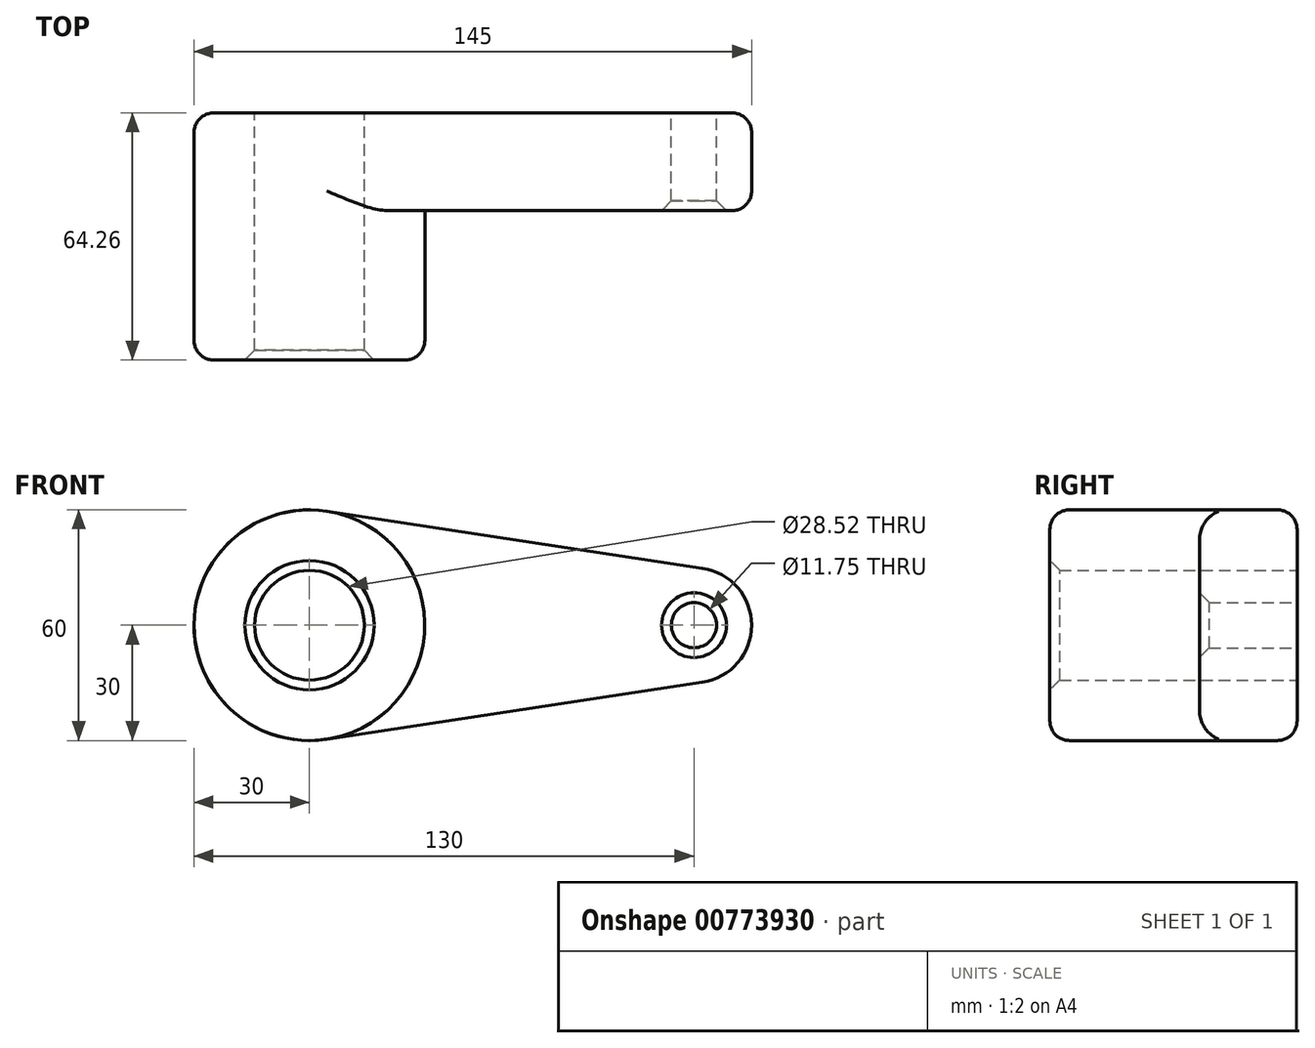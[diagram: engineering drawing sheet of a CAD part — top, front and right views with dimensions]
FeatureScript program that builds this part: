
annotation { "Feature Type Name" : "Feature", "Feature Type Description" : "" }
export const myFeature = defineFeature(function(context is Context, id is Id, definition is map)
    precondition{}
    {
        {
            var Q0;
            Q0=qCreatedBy(makeId("Front.planeOp"),FACE);
            var sketch = newSketch(context, id + "F0", { "sketchPlane" : qUnion([Q0])});
            skCircle(sketch, "E0", {"center": v(0, 0) * mm, "radius": 30 * mm});
            skCircle(sketch, "E1", {"center": v(100, 0) * mm, "radius": 15 * mm});
            skLineSegment(sketch, "E2", {"start": v(4.5, 29.66) * mm, "end": v(102.25, 14.83) * mm});
            skLineSegment(sketch, "E3", {"start": v(4.5, -29.66) * mm, "end": v(102.25, -14.83) * mm});
            skCircle(sketch, "E4", {"center": v(0, 0) * mm, "radius": 14.26 * mm});
            skCircle(sketch, "E5", {"center": v(100, 0) * mm, "radius": 5.87 * mm});
            skSolve(sketch);
        }
        {
            var Q0;
            Q0 = qSketchRegion(id + "F0", true);
            extrude(context, id + "F1", {"entities" : qUnion([Q0]), "depth" : 25.4 * mm, "offsetDistance" : 25.4 * mm});
        }
        {
            var Q0;
            Q0=makeQuery(id+"F0.imprint","IMPRINT",FACE,{"disambiguationData":[TD([[makeQuery(id+"F0.imprint","IMPRINT",EDGE,{"derivedFrom":sQuery(id+"F0.wireOp",EDGE,"E4")}),-1.0]])]});
            extrude(context, id + "F2", {"entities" : qUnion([Q0]), "operationType" : NewBodyOperationType.ADD, "depth" : 64.26 * mm, "offsetDistance" : 25.4 * mm});
        }
        {
            var Q0;
            Q0=makeQuery(id+"F1.opExtrude","CAP_EDGE",EDGE,{"disambiguationData":[OSD([sQuery(id+"F0.wireOp",EDGE,"E3")])],"isStart":true});
            var Q1;
            Q1=makeQuery(id+"F2.opExtrude","CAP_EDGE",EDGE,{"disambiguationData":[OSD([sQuery(id+"F0.wireOp",EDGE,"E0")])],"isStart":false});
            fillet(context, id + "F3", {"entities" : qUnion([Q0, Q1]), "radius" : 5.08 * mm, "tangentPropagation" : true, "allowEdgeOverflow" : false});
        }
        {
            var Q0;
            Q0=makeQuery(id+"F1.opExtrude","CAP_EDGE",EDGE,{"disambiguationData":[OSD([sQuery(id+"F0.wireOp",EDGE,"E3")])],"isStart":false});
            var Q1;
            Q1=makeQuery(id+"F1.opExtrude","CAP_EDGE",EDGE,{"disambiguationData":[OSD([sQuery(id+"F0.wireOp",EDGE,"E2")])],"isStart":false});
            fillet(context, id + "F4", {"entities" : qUnion([Q0, Q1]), "radius" : 5.08 * mm, "tangentPropagation" : true, "allowEdgeOverflow" : false});
        }
        {
            var Q0;
            Q0=makeQuery(id+"F2.opExtrude","CAP_EDGE",EDGE,{"disambiguationData":[OSD([sQuery(id+"F0.wireOp",EDGE,"E4")])],"isStart":false});
            var Q1;
            Q1=makeQuery(id+"F1.opExtrude","CAP_EDGE",EDGE,{"disambiguationData":[OSD([sQuery(id+"F0.wireOp",EDGE,"E5")])],"isStart":false});
            chamfer(context, id + "F5", {"entities" : qUnion([Q0, Q1]), "width" : 2.54 * mm, "tangentPropagation" : true});
        }
    });
